# Revit family: Sanitary_Taps&Mixers_Zurn_Z875L7_Wall-Mounted
name_source: partatom
category: Plumbing Fixtures
units: mm (PartAtom-declared; Revit-internal decimal feet)

## family parameters
Cut with Voids When Loaded = No
Host = Face
Maintain Annotation Orientation = No
OmniClass Number = 23.45.55.14
OmniClass Title = Single Faucets
Part Type = Normal
Room Calculation Point = No
Round Connector Dimension = Use Radius
Shared = No

## types (1)
- Z875L7
    ADA Compliance = No
    Assembly Code = D2010
    CW Connection = Yes
    CWFU = 1
    Center to Handle = 2 1/2"
    Default Elevation = 48"
    Description = WALL MOUNTED LABORATORY FITTING
    Distance Between Center to end = 3 1/2"
    Distance between Centerset = 3"
    Flow Rate = 0.0 GPM
    HW Connection = No
    HWFU = 0
    Inlet Connection Size (inch) = 1/2"
    Lead-Free Compliant = No
    Manufacturer = Zurn water, LLC
    Manufacturer Brand = Zurn
    Model = Z875L7
    Modified Date = 10/24/2025
    Product Documentation Link = http://www.zurn.com
    Product Material = Brass - Zurn - Polished Chrome-Finish
    Product Page URL = https://www.zurn.com
    Product data URL = https://bimobject.com
    Spout Reach = 6"
    URL = http://www.zurn.com
    Vent Connection = No
    WFU = 0
    Waste Connection = No
    Water Sense Compliance = No

## geometry (parser evidence)
native form markers: Sweep x6
no freeform markers — native parametric forms only
